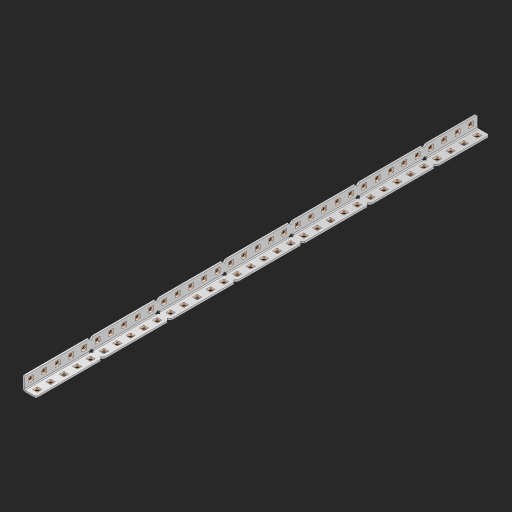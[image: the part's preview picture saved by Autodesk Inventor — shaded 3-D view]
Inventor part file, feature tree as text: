
AUTODESK INVENTOR PART (.ipt)
format: ipt  version: 2023 (Build 270158000, 158)  size: 1,106,432 bytes
history: native  units: in
note: dims shown in document units (in); Inventor stores cm internally (conversion verified against a paired STEP export)
features: other x74, extrude x69, sheet_metal_op x8, sketch x5, pattern_linear x1, mirror x1, chamfer x1
ambient origin geometry x8: Origin, YZ Plane, XZ Plane, XY Plane, X Axis, Y Axis, Z Axis, Center Point
bodies: Solid1 (feature_tree), Body (feature_tree)
feature tree (159):
  sheet_metal_op  "Flanges"
  sheet_metal_op  "Body Pattern"
  other  "Arc Length"
  pattern_linear  "Notch Pattern"  Spacing1=0.125in  [1 undecoded]
  other  "Diagonal Plane"
  mirror  "Everything Mirrored"
  chamfer  "End Chamfer"
  sketch  "Sketch1"  dims[d0=0.5in]
  other  "Plate1"
  sketch  "Sketch2"  dims[d1=17.0in]
  other  "Plate2"
  sheet_metal_op  "Bend1"
  sheet_metal_op  "Corner1"
  sketch  "Sketch8"  dims[d2=0.0625in]
  sketch  "Sketch9"  dims[d3=0.0625in]
  other  "Srf91"
  sheet_metal_op  "Body Pattern Sketch"
  other  "Srf92"
  sketch  "Sketch13"  dims[d4=0.0312in d5=0.125in d6=0.0625in d7=0.5in d8=90.0deg d9=0.0312in d10=0.25in d11=0.0625in d12=0.0625in d49=0.182in d50=0.02in d52=0.25in d53=0.0625in d54=0.0in d55=0.172in d56=1.0in d57=0.0in d85=0.1473in d86=0.1782in d89=0.0625in d90=0.0in d91=0.04in d92=0.0491in d95=2.5in d96=0.04in d97=0.25in d98=45.0deg d123=0.204in d126=0.0491in d127=0.1473in d128=0.08in d129=0.04in d130=2.5in d131=13.3858in d133=0.5in d134=0.3937in d136=1.0in]
  other  "Srf856"
  other  "Srf857"
  other  "Srf858"
  other  "Srf859"
  other  "Srf860"
  other  "Srf861"
  other  "Srf1275"
  other  "Srf1276"
  other  "Srf1278"
  other  "Srf1279"
  other  "Srf1280"
  other  "Srf1281"
  other  "Srf1282"
  other  "Srf1283"
  other  "Srf1383"
  other  "Srf1384"
  other  "Srf1385"
  other  "Srf1386"
  other  "Srf1387"
  other  "Srf1388"
  other  "Srf1389"
  other  "Srf1390"
  other  "Srf1391"
  other  "Srf1392"
  other  "Srf1393"
  other  "Srf1394"
  other  "Srf1395"
  other  "Srf1396"
  other  "Srf1397"
  other  "Srf1398"
  other  "Srf1399"
  other  "Srf1400"
  other  "Srf1401"
  other  "Srf1402"
  other  "Srf1403"
  other  "Srf1404"
  other  "Srf1405"
  other  "Srf1406"
  other  "Srf1407"
  other  "Srf1408"
  other  "Srf1409"
  other  "Srf1475"
  other  "Srf1476"
  other  "Srf1477"
  other  "Srf1478"
  other  "Srf1479"
  other  "Srf1480"
  other  "Srf1481"
  other  "Srf1482"
  other  "Srf1483"
  other  "Srf1484"
  other  "Srf1485"
  other  "Srf1486"
  other  "Srf1487"
  other  "Srf1488"
  other  "Srf1489"
  other  "Srf1490"
  other  "Srf1491"
  other  "Srf1492"
  other  "Srf1493"
  other  "Srf1494"
  other  "Srf1495"
  other  "Srf1496"
  other  "Srf1497"
  other  "Srf1498"
  other  "Srf1499"
  other  "Srf1500"
  other  "Srf1501"
  sheet_metal_op  "Body Stamp"
  sheet_metal_op  "Body Circle"
  sheet_metal_op  "Notch"
  extrude  "ExtrusionSrf92"  Depth=0.0625in
  extrude  "ExtrusionSrf856"  Depth=0.5in TaperAngle=90.0deg
  extrude  "ExtrusionSrf857"  Depth=0.25in
  extrude  "ExtrusionSrf858"  Depth=0.0625in
  extrude  "ExtrusionSrf859"  Depth=0.0625in
  extrude  "ExtrusionSrf860"  Depth=0.3937in
  extrude  "ExtrusionSrf861"  Depth=0.02in
  extrude  "ExtrusionSrf1275"  Depth=0.25in
  extrude  "ExtrusionSrf1276"  Depth=0.0625in
  extrude  "ExtrusionSrf1277"  TaperAngle=0.0deg  [1 undecoded]
  extrude  "ExtrusionSrf1278"  Depth=0.3937in
  extrude  "ExtrusionSrf1279"  Depth=0.3937in TaperAngle=0.0deg
  extrude  "ExtrusionSrf1280"  Depth=0.3937in
  extrude  "ExtrusionSrf1281"  Depth=0.3937in
  extrude  "ExtrusionSrf1282"  Depth=0.0625in
  extrude  "ExtrusionSrf1383"  Depth=0.3937in TaperAngle=0.0deg
  extrude  "ExtrusionSrf1384"  Depth=0.3937in
  extrude  "ExtrusionSrf1385"  Depth=0.25in TaperAngle=45.0deg
  extrude  "ExtrusionSrf1386"  Depth=0.3937in
  extrude  "ExtrusionSrf1387"  Depth=0.3937in
  extrude  "ExtrusionSrf1388"  Depth=0.3937in
  extrude  "ExtrusionSrf1389"  Depth=0.3937in
  extrude  "ExtrusionSrf1390"  Depth=0.3937in
  extrude  "ExtrusionSrf1391"  Depth=0.3937in
  extrude  "ExtrusionSrf1392"  Depth=0.3937in
  extrude  "ExtrusionSrf1393"  Depth=0.5in
  extrude  "ExtrusionSrf1394"  [1 undecoded]
  extrude  "ExtrusionSrf1395"  [1 undecoded]
  extrude  "ExtrusionSrf1396"  [1 undecoded]
  extrude  "ExtrusionSrf1397"  [1 undecoded]
  extrude  "ExtrusionSrf1398"  [1 undecoded]
  extrude  "ExtrusionSrf1399"  [1 undecoded]
  extrude  "ExtrusionSrf1400"  [1 undecoded]
  extrude  "ExtrusionSrf1401"  [1 undecoded]
  extrude  "ExtrusionSrf1402"  [1 undecoded]
  extrude  "ExtrusionSrf1403"  [1 undecoded]
  extrude  "ExtrusionSrf1404"  [1 undecoded]
  extrude  "ExtrusionSrf1405"  [1 undecoded]
  extrude  "ExtrusionSrf1406"  [1 undecoded]
  extrude  "ExtrusionSrf1407"  [1 undecoded]
  extrude  "ExtrusionSrf1408"  [1 undecoded]
  extrude  "ExtrusionSrf1409"  [1 undecoded]
  extrude  "ExtrusionSrf1475"  [1 undecoded]
  extrude  "ExtrusionSrf1476"  [1 undecoded]
  extrude  "ExtrusionSrf1477"  [1 undecoded]
  extrude  "ExtrusionSrf1478"  [1 undecoded]
  extrude  "ExtrusionSrf1479"  [1 undecoded]
  extrude  "ExtrusionSrf1480"  [1 undecoded]
  extrude  "ExtrusionSrf1481"  [1 undecoded]
  extrude  "ExtrusionSrf1482"  [1 undecoded]
  extrude  "ExtrusionSrf1483"  [1 undecoded]
  extrude  "ExtrusionSrf1484"  [1 undecoded]
  extrude  "ExtrusionSrf1485"  [1 undecoded]
  extrude  "ExtrusionSrf1486"  [1 undecoded]
  extrude  "ExtrusionSrf1487"  [1 undecoded]
  extrude  "ExtrusionSrf1488"  [1 undecoded]
  extrude  "ExtrusionSrf1489"  [1 undecoded]
  extrude  "ExtrusionSrf1490"  [1 undecoded]
  extrude  "ExtrusionSrf1491"  [1 undecoded]
  extrude  "ExtrusionSrf1492"  [1 undecoded]
  extrude  "ExtrusionSrf1493"  [1 undecoded]
  extrude  "ExtrusionSrf1494"  [1 undecoded]
  extrude  "ExtrusionSrf1495"  [1 undecoded]
  extrude  "ExtrusionSrf1496"  [1 undecoded]
  extrude  "ExtrusionSrf1497"  [1 undecoded]
  extrude  "ExtrusionSrf1498"  [1 undecoded]
  extrude  "ExtrusionSrf1499"  [1 undecoded]
  extrude  "ExtrusionSrf1500"  [1 undecoded]
  extrude  "ExtrusionSrf1501"  [1 undecoded]
note: 45 required parameter values undecoded (feature->parameter linkage not recoverable at this tier; creation-order binding heuristic only, values carry confidence <= 0.55)
